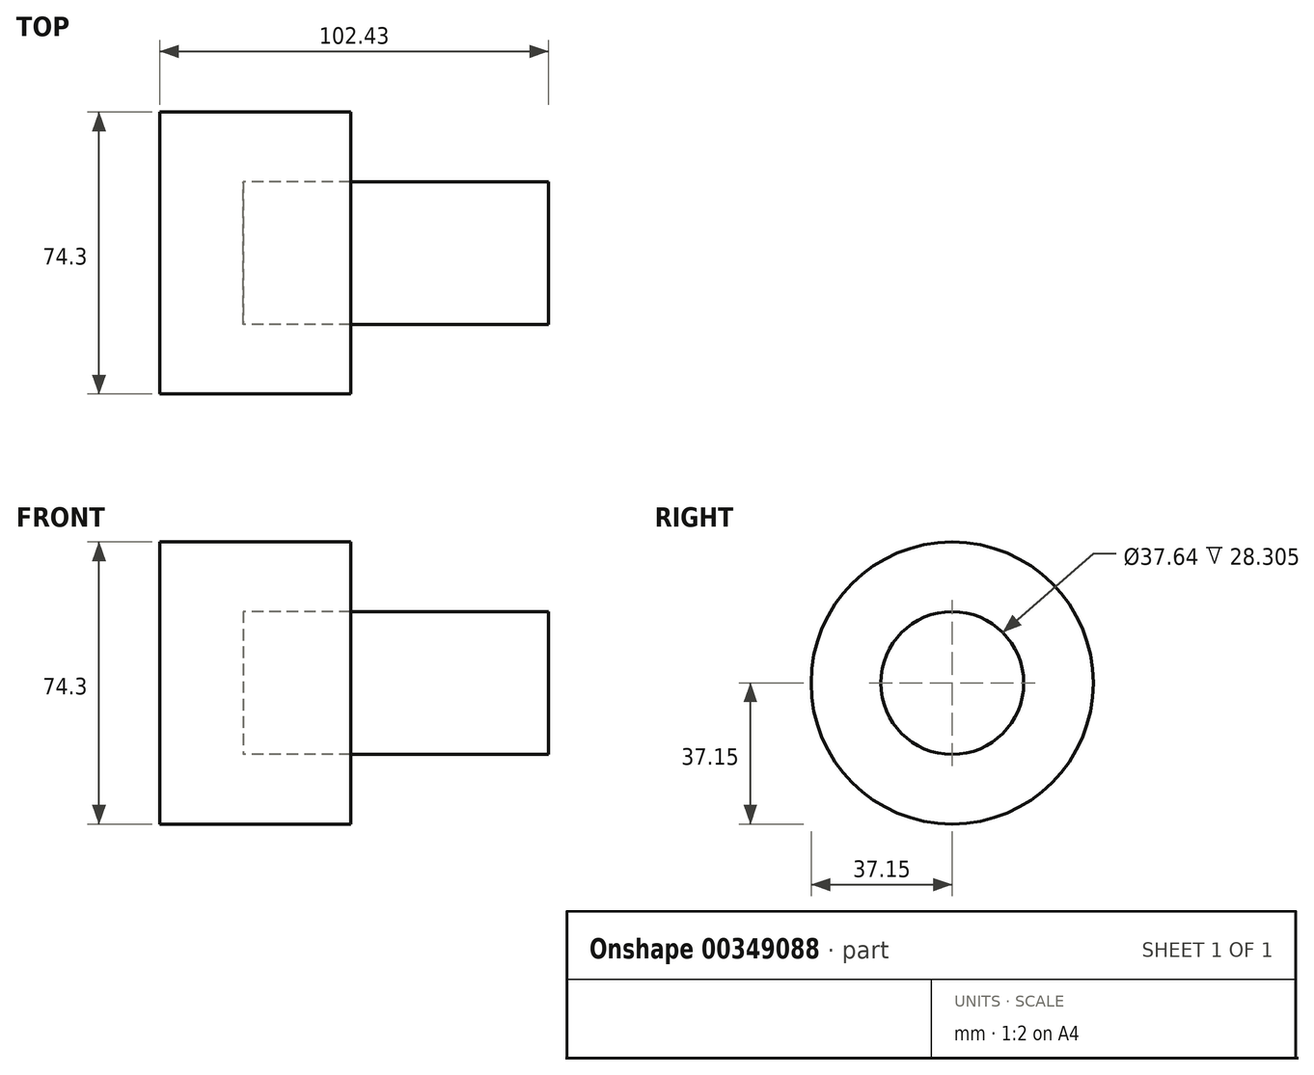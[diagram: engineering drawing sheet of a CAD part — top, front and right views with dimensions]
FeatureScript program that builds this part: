
annotation { "Feature Type Name" : "Feature", "Feature Type Description" : "" }
export const myFeature = defineFeature(function(context is Context, id is Id, definition is map)
    precondition{}
    {
        {
            var Q0;
            Q0=qCreatedBy(makeId("Top.planeOp"),FACE);
            var sketch = newSketch(context, id + "F0", { "sketchPlane" : qUnion([Q0])});
            skLineSegment(sketch, "E0", {"start": v(0, 0) * mm, "end": v(50.28, 0) * mm});
            skLineSegment(sketch, "E1", {"start": v(50.28, 0) * mm, "end": v(50.28, 37.15) * mm});
            skLineSegment(sketch, "E2", {"start": v(50.28, 37.15) * mm, "end": v(0, 37.15) * mm});
            skLineSegment(sketch, "E3", {"start": v(0, 37.15) * mm, "end": v(0, 0) * mm});
            skLineSegment(sketch, "E4", {"start": v(50.28, 0) * mm, "end": v(102.43, 0) * mm});
            skLineSegment(sketch, "E5", {"start": v(102.43, 0) * mm, "end": v(102.43, 18.82) * mm});
            skLineSegment(sketch, "E6", {"start": v(102.43, 18.82) * mm, "end": v(21.98, 18.82) * mm});
            skLineSegment(sketch, "E7", {"start": v(21.98, 18.82) * mm, "end": v(21.98, 0) * mm});
            skSolve(sketch);
        }
        {
            var Q0;
            {var subQ0=sQuery(id+"F0.wireOp",EDGE,"E2");Q0=makeQuery(id+"F0.imprint","IMPRINT",FACE,{"disambiguationData":[TD([[makeQuery(id+"F0.imprint","IMPRINT",EDGE,{"derivedFrom":subQ0}),1.0]])]});}
            var Q1;
            Q1=sQuery(id+"F0.wireOp",EDGE,"E0");
            revolve(context, id + "F1", {"entities" : qUnion([Q0]), "axis" : qUnion([Q1]), "revolveType" : RevolveType.FULL});
        }
        {
            var Q0;
            {var subQ0=sQuery(id+"F0.wireOp",EDGE,"E4");Q0=makeQuery(id+"F0.imprint","IMPRINT",FACE,{"disambiguationData":[TD([[makeQuery(id+"F0.imprint","IMPRINT",EDGE,{"derivedFrom":subQ0}),1.0]])]});}
            var Q1;
            Q1=sQuery(id+"F0.wireOp",EDGE,"E4");
            revolve(context, id + "F2", {"entities" : qUnion([Q0]), "axis" : qUnion([Q1]), "revolveType" : RevolveType.FULL});
        }
    });
